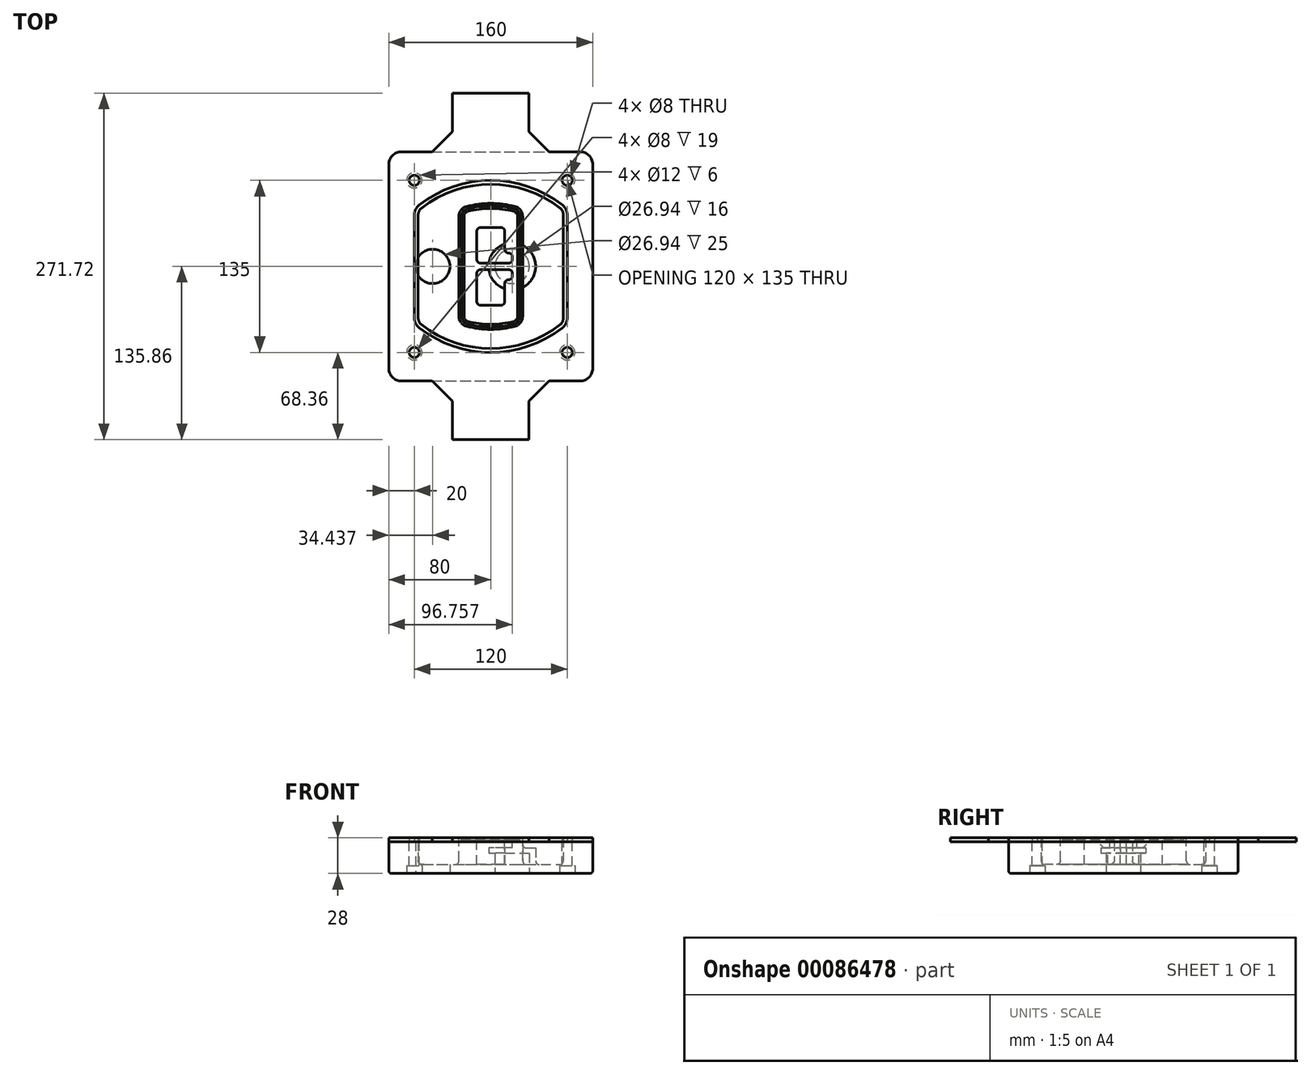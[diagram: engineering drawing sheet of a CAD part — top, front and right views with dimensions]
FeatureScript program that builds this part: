
annotation { "Feature Type Name" : "Feature", "Feature Type Description" : "" }
export const myFeature = defineFeature(function(context is Context, id is Id, definition is map)
    precondition{}
    {
        {
            var Q0;
            Q0=qCreatedBy(makeId("Top.planeOp"),FACE);
            var sketch = newSketch(context, id + "F0", { "sketchPlane" : qUnion([Q0])});
            skPoint(sketch, "E0.rect.middle", {"position": v(0, 0) * mm});
            skLineSegment(sketch, "E1.bottom", {"start": v(-70, -90) * mm, "end": v(70, -90) * mm});
            skLineSegment(sketch, "E1.top", {"start": v(-70, 90) * mm, "end": v(70, 90) * mm});
            skLineSegment(sketch, "E1.left", {"start": v(-80, -80) * mm, "end": v(-80, 80) * mm});
            skLineSegment(sketch, "E1.right", {"start": v(80, -80) * mm, "end": v(80, 80) * mm});
            skLineSegment(sketch, "E2", {"start": v(-80, 90) * mm, "end": v(80, -90) * mm, "construction": true});
            skLineSegment(sketch, "E3", {"start": v(80, 90) * mm, "end": v(-80, -90) * mm, "construction": true});
            skCircle(sketch, "E4", {"center": v(-60, 67.5) * mm, "radius": 4 * mm});
            skCircle(sketch, "E5", {"center": v(60, 67.5) * mm, "radius": 4 * mm});
            skCircle(sketch, "E6", {"center": v(60, -67.5) * mm, "radius": 4 * mm});
            skCircle(sketch, "E7", {"center": v(-60, -67.5) * mm, "radius": 4 * mm});
            skLineSegment(sketch, "E8", {"start": v(-60, 67.5) * mm, "end": v(60, 67.5) * mm, "construction": true});
            skLineSegment(sketch, "E9", {"start": v(60, 67.5) * mm, "end": v(60, -67.5) * mm, "construction": true});
            skLineSegment(sketch, "E10", {"start": v(60, -67.5) * mm, "end": v(-60, -67.5) * mm, "construction": true});
            skLineSegment(sketch, "E11", {"start": v(-60, -67.5) * mm, "end": v(-60, 67.5) * mm, "construction": true});
            skLineSegment(sketch, "E12", {"start": v(-60, 40.3) * mm, "end": v(-60, -40.3) * mm});
            skLineSegment(sketch, "E13", {"start": v(60, 40.3) * mm, "end": v(60, -40.3) * mm});
            skArc(sketch, "E14", {"start": v(56.15, 48.18) * mm, "mid": v(0, 67.5) * mm, "end": v(-56.15, 48.18) * mm});
            skArc(sketch, "E15", {"start": v(-56.15, -48.18) * mm, "mid": v(0, -67.5) * mm, "end": v(56.15, -48.18) * mm});
            skLineSegment(sketch, "E16", {"start": v(-60, 0) * mm, "end": v(60, 0) * mm, "construction": true});
            skPoint(sketch, "E17.visualSharp", {"position": v(-60, -45) * mm});
            skArc(sketch, "E17.filletArc", {"start": v(-60, -40.3) * mm, "mid": v(-58.99, -44.68) * mm, "end": v(-56.15, -48.18) * mm});
            skPoint(sketch, "E18.visualSharp", {"position": v(-60, 45) * mm});
            skArc(sketch, "E18.filletArc", {"start": v(-56.15, 48.18) * mm, "mid": v(-58.99, 44.68) * mm, "end": v(-60, 40.3) * mm});
            skPoint(sketch, "E19.visualSharp", {"position": v(60, 45) * mm});
            skArc(sketch, "E19.filletArc", {"start": v(60, 40.3) * mm, "mid": v(58.99, 44.68) * mm, "end": v(56.15, 48.18) * mm});
            skPoint(sketch, "E20.visualSharp", {"position": v(60, -45) * mm});
            skArc(sketch, "E20.filletArc", {"start": v(56.15, -48.18) * mm, "mid": v(58.99, -44.68) * mm, "end": v(60, -40.3) * mm});
            skPoint(sketch, "E21.visualSharp", {"position": v(-80, 90) * mm});
            skArc(sketch, "E21.filletArc", {"start": v(-70, 90) * mm, "mid": v(-77.07, 87.07) * mm, "end": v(-80, 80) * mm});
            skPoint(sketch, "E22.visualSharp", {"position": v(80, 90) * mm});
            skArc(sketch, "E22.filletArc", {"start": v(80, 80) * mm, "mid": v(77.07, 87.07) * mm, "end": v(70, 90) * mm});
            skPoint(sketch, "E23.visualSharp", {"position": v(80, -90) * mm});
            skArc(sketch, "E23.filletArc", {"start": v(70, -90) * mm, "mid": v(77.07, -87.07) * mm, "end": v(80, -80) * mm});
            skPoint(sketch, "E24.visualSharp", {"position": v(-80, -90) * mm});
            skArc(sketch, "E24.filletArc", {"start": v(-80, -80) * mm, "mid": v(-77.07, -87.07) * mm, "end": v(-70, -90) * mm});
            skArc(sketch, "E25.0", {"start": v(57, 40.3) * mm, "mid": v(56.3, 43.36) * mm, "end": v(54.3, 45.81) * mm});
            skLineSegment(sketch, "E25.1", {"start": v(57, 40.3) * mm, "end": v(57, -40.3) * mm});
            skArc(sketch, "E25.2", {"start": v(54.3, -45.81) * mm, "mid": v(56.3, -43.36) * mm, "end": v(57, -40.3) * mm});
            skArc(sketch, "E25.3", {"start": v(-54.3, -45.81) * mm, "mid": v(0, -64.5) * mm, "end": v(54.3, -45.81) * mm});
            skArc(sketch, "E25.4", {"start": v(-57, -40.3) * mm, "mid": v(-56.3, -43.36) * mm, "end": v(-54.3, -45.81) * mm});
            skArc(sketch, "E25.5", {"start": v(54.3, 45.81) * mm, "mid": v(0, 64.5) * mm, "end": v(-54.3, 45.81) * mm});
            skLineSegment(sketch, "E25.6", {"start": v(-57, 40.3) * mm, "end": v(-57, -40.3) * mm});
            skArc(sketch, "E25.7", {"start": v(-54.3, 45.81) * mm, "mid": v(-56.3, 43.36) * mm, "end": v(-57, 40.3) * mm});
            skArc(sketch, "E26.0", {"start": v(-58.62, 51.33) * mm, "mid": v(-62.58, 46.43) * mm, "end": v(-64, 40.3) * mm});
            skArc(sketch, "E26.1", {"start": v(58.62, 51.33) * mm, "mid": v(0, 71.5) * mm, "end": v(-58.62, 51.33) * mm});
            skArc(sketch, "E26.2", {"start": v(64, 40.3) * mm, "mid": v(62.58, 46.43) * mm, "end": v(58.62, 51.33) * mm});
            skLineSegment(sketch, "E26.3", {"start": v(64, 40.3) * mm, "end": v(64, -40.3) * mm});
            skArc(sketch, "E26.4", {"start": v(58.62, -51.33) * mm, "mid": v(62.58, -46.43) * mm, "end": v(64, -40.3) * mm});
            skLineSegment(sketch, "E26.5", {"start": v(-64, 40.3) * mm, "end": v(-64, -40.3) * mm});
            skArc(sketch, "E26.6", {"start": v(-58.62, -51.33) * mm, "mid": v(0, -71.5) * mm, "end": v(58.62, -51.33) * mm});
            skArc(sketch, "E26.7", {"start": v(-64, -40.3) * mm, "mid": v(-62.58, -46.43) * mm, "end": v(-58.62, -51.33) * mm});
            skSolve(sketch);
        }
        {
            var Q0;
            Q0=makeQuery(id+"F0.imprint","IMPRINT",FACE,{"disambiguationData":[TD([[makeQuery(id+"F0.imprint","IMPRINT",EDGE,{"derivedFrom":sQuery(id+"F0.wireOp",EDGE,"E1.bottom")}),1.0]])]});
            var Q1;
            Q1=makeQuery(id+"F0.imprint","IMPRINT",FACE,{"disambiguationData":[TD([[makeQuery(id+"F0.imprint","IMPRINT",EDGE,{"derivedFrom":sQuery(id+"F0.wireOp",EDGE,"E12")}),1.0]])]});
            var Q2;
            Q2=makeQuery(id+"F0.imprint","IMPRINT",FACE,{"disambiguationData":[TD([[makeQuery(id+"F0.imprint","IMPRINT",EDGE,{"derivedFrom":sQuery(id+"F0.wireOp",EDGE,"E25.0")}),1.0]])]});
            var Q3;
            Q3=makeQuery(id+"F0.imprint","IMPRINT",FACE,{"disambiguationData":[TD([[makeQuery(id+"F0.imprint","IMPRINT",EDGE,{"derivedFrom":sQuery(id+"F0.wireOp",EDGE,"E12")}),-1.0]])]});
            extrude(context, id + "F1", {"entities" : qUnion([Q0, Q1, Q2, Q3]), "oppositeDirection" : true, "depth" : 25 * mm});
        }
        {
            var Q0;
            Q0=makeQuery(id+"F0.imprint","IMPRINT",FACE,{"disambiguationData":[TD([[makeQuery(id+"F0.imprint","IMPRINT",EDGE,{"derivedFrom":sQuery(id+"F0.wireOp",EDGE,"E12")}),1.0]])]});
            extrude(context, id + "F2", {"entities" : qUnion([Q0]), "operationType" : NewBodyOperationType.ADD, "depth" : 3 * mm});
        }
        {
            var Q0;
            Q0=makeQuery(id+"F0.imprint","IMPRINT",FACE,{"disambiguationData":[TD([[makeQuery(id+"F0.imprint","IMPRINT",EDGE,{"derivedFrom":sQuery(id+"F0.wireOp",EDGE,"E25.0")}),1.0]])]});
            extrude(context, id + "F3", {"entities" : qUnion([Q0]), "operationType" : NewBodyOperationType.REMOVE, "oppositeDirection" : true, "depth" : 18 * mm});
        }
        {
            var Q0;
            Q0=makeQuery(id+"F2.opExtrude","CAP_FACE",FACE,{"disambiguationData":[OSD([sQuery(id+"F0.wireOp",EDGE,"E12"),sQuery(id+"F0.wireOp",EDGE,"E13"),sQuery(id+"F0.wireOp",EDGE,"E14"),sQuery(id+"F0.wireOp",EDGE,"E15"),sQuery(id+"F0.wireOp",EDGE,"E17.filletArc"),sQuery(id+"F0.wireOp",EDGE,"E18.filletArc"),sQuery(id+"F0.wireOp",EDGE,"E19.filletArc"),sQuery(id+"F0.wireOp",EDGE,"E20.filletArc"),sQuery(id+"F0.wireOp",EDGE,"E25.0"),sQuery(id+"F0.wireOp",EDGE,"E25.1"),sQuery(id+"F0.wireOp",EDGE,"E25.2"),sQuery(id+"F0.wireOp",EDGE,"E25.3"),sQuery(id+"F0.wireOp",EDGE,"E25.4"),sQuery(id+"F0.wireOp",EDGE,"E25.5"),sQuery(id+"F0.wireOp",EDGE,"E25.6"),sQuery(id+"F0.wireOp",EDGE,"E25.7")])],"isStart":false});
            var sketch = newSketch(context, id + "F4", { "sketchPlane" : qUnion([Q0])});
            skArc(sketch, "E27.0", {"start": v(-19.08, -46.97) * mm, "mid": v(0, -49.5) * mm, "end": v(19.08, -46.97) * mm});
            skArc(sketch, "E28.0", {"start": v(19.08, 46.97) * mm, "mid": v(0, 49.5) * mm, "end": v(-19.08, 46.97) * mm});
            skLineSegment(sketch, "E29", {"start": v(-25, 39.25) * mm, "end": v(-25, -39.25) * mm});
            skLineSegment(sketch, "E30", {"start": v(25, 39.25) * mm, "end": v(25, -39.25) * mm});
            skLineSegment(sketch, "E31", {"start": v(-25, 45.1) * mm, "end": v(25, 45.1) * mm, "construction": true});
            skLineSegment(sketch, "E32", {"start": v(-25, -45.1) * mm, "end": v(25, -45.1) * mm, "construction": true});
            skPoint(sketch, "E33.visualSharp", {"position": v(-25, 45.1) * mm});
            skArc(sketch, "E33.filletArc", {"start": v(-19.08, 46.97) * mm, "mid": v(-23.35, 44.11) * mm, "end": v(-25, 39.25) * mm});
            skPoint(sketch, "E34.visualSharp", {"position": v(25, 45.1) * mm});
            skArc(sketch, "E34.filletArc", {"start": v(25, 39.25) * mm, "mid": v(23.35, 44.11) * mm, "end": v(19.08, 46.97) * mm});
            skPoint(sketch, "E35.visualSharp", {"position": v(25, -45.1) * mm});
            skArc(sketch, "E35.filletArc", {"start": v(19.08, -46.97) * mm, "mid": v(23.35, -44.11) * mm, "end": v(25, -39.25) * mm});
            skPoint(sketch, "E36.visualSharp", {"position": v(-25, -45.1) * mm});
            skArc(sketch, "E36.filletArc", {"start": v(-25, -39.25) * mm, "mid": v(-23.35, -44.11) * mm, "end": v(-19.08, -46.97) * mm});
            skArc(sketch, "E37.0", {"start": v(54.3, 45.81) * mm, "mid": v(0, 64.5) * mm, "end": v(-54.3, 45.81) * mm});
            skArc(sketch, "E37.1", {"start": v(-54.3, 45.81) * mm, "mid": v(-56.3, 43.36) * mm, "end": v(-57, 40.3) * mm});
            skLineSegment(sketch, "E37.2", {"start": v(-57, 40.3) * mm, "end": v(-57, -40.3) * mm});
            skArc(sketch, "E37.3", {"start": v(-57, -40.3) * mm, "mid": v(-56.3, -43.36) * mm, "end": v(-54.3, -45.81) * mm});
            skArc(sketch, "E37.4", {"start": v(-54.3, -45.81) * mm, "mid": v(0, -64.5) * mm, "end": v(54.3, -45.81) * mm});
            skArc(sketch, "E37.5", {"start": v(54.3, -45.81) * mm, "mid": v(56.3, -43.36) * mm, "end": v(57, -40.3) * mm});
            skLineSegment(sketch, "E37.6", {"start": v(57, 40.3) * mm, "end": v(57, -40.3) * mm});
            skArc(sketch, "E37.7", {"start": v(57, 40.3) * mm, "mid": v(56.3, 43.36) * mm, "end": v(54.3, 45.81) * mm});
            skLineSegment(sketch, "E38.0", {"start": v(23, 39.25) * mm, "end": v(23, -39.25) * mm});
            skArc(sketch, "E38.1", {"start": v(18.56, -45.04) * mm, "mid": v(21.76, -42.9) * mm, "end": v(23, -39.25) * mm});
            skArc(sketch, "E38.2", {"start": v(-18.56, -45.04) * mm, "mid": v(0, -47.5) * mm, "end": v(18.56, -45.04) * mm});
            skArc(sketch, "E38.3", {"start": v(-23, -39.25) * mm, "mid": v(-21.76, -42.9) * mm, "end": v(-18.56, -45.04) * mm});
            skLineSegment(sketch, "E38.4", {"start": v(-23, 39.25) * mm, "end": v(-23, -39.25) * mm});
            skArc(sketch, "E38.5", {"start": v(23, 39.25) * mm, "mid": v(21.76, 42.9) * mm, "end": v(18.56, 45.04) * mm});
            skArc(sketch, "E38.6", {"start": v(-18.56, 45.04) * mm, "mid": v(-21.76, 42.9) * mm, "end": v(-23, 39.25) * mm});
            skArc(sketch, "E38.7", {"start": v(18.56, 45.04) * mm, "mid": v(0, 47.5) * mm, "end": v(-18.56, 45.04) * mm});
            skArc(sketch, "E39.0", {"start": v(21, 39.25) * mm, "mid": v(20.18, 41.68) * mm, "end": v(18.04, 43.1) * mm});
            skLineSegment(sketch, "E39.1", {"start": v(21, 39.25) * mm, "end": v(21, -39.25) * mm});
            skArc(sketch, "E39.2", {"start": v(18.04, -43.1) * mm, "mid": v(20.18, -41.68) * mm, "end": v(21, -39.25) * mm});
            skArc(sketch, "E39.3", {"start": v(-18.04, -43.1) * mm, "mid": v(0, -45.5) * mm, "end": v(18.04, -43.1) * mm});
            skArc(sketch, "E39.4", {"start": v(-21, -39.25) * mm, "mid": v(-20.18, -41.68) * mm, "end": v(-18.04, -43.1) * mm});
            skArc(sketch, "E39.5", {"start": v(18.04, 43.1) * mm, "mid": v(0, 45.5) * mm, "end": v(-18.04, 43.1) * mm});
            skLineSegment(sketch, "E39.6", {"start": v(-21, 39.25) * mm, "end": v(-21, -39.25) * mm});
            skArc(sketch, "E39.7", {"start": v(-18.04, 43.1) * mm, "mid": v(-20.18, 41.68) * mm, "end": v(-21, 39.25) * mm});
            skLineSegment(sketch, "E40", {"start": v(-25, 0) * mm, "end": v(25, 0) * mm, "construction": true});
            skLineSegment(sketch, "E41", {"start": v(-11, 5.5) * mm, "end": v(-11, 27.5) * mm});
            skLineSegment(sketch, "E42", {"start": v(-8, 30.5) * mm, "end": v(8, 30.5) * mm});
            skLineSegment(sketch, "E43", {"start": v(11, 27.5) * mm, "end": v(11, 13.5) * mm});
            skLineSegment(sketch, "E44", {"start": v(14, 10.5) * mm, "end": v(14, 10.5) * mm});
            skLineSegment(sketch, "E45", {"start": v(17, 7.5) * mm, "end": v(17, 5.5) * mm});
            skLineSegment(sketch, "E46", {"start": v(14, 2.5) * mm, "end": v(-8, 2.5) * mm});
            skPoint(sketch, "E47.visualSharp", {"position": v(-11, 30.5) * mm});
            skArc(sketch, "E47.filletArc", {"start": v(-8, 30.5) * mm, "mid": v(-10.12, 29.62) * mm, "end": v(-11, 27.5) * mm});
            skPoint(sketch, "E48.visualSharp", {"position": v(11, 30.5) * mm});
            skArc(sketch, "E48.filletArc", {"start": v(11, 27.5) * mm, "mid": v(10.12, 29.62) * mm, "end": v(8, 30.5) * mm});
            skPoint(sketch, "E49.visualSharp", {"position": v(11, 10.5) * mm});
            skArc(sketch, "E49.filletArc", {"start": v(11, 13.5) * mm, "mid": v(11.88, 11.38) * mm, "end": v(14, 10.5) * mm});
            skPoint(sketch, "E50.visualSharp", {"position": v(17, 10.5) * mm});
            skArc(sketch, "E50.filletArc", {"start": v(17, 7.5) * mm, "mid": v(16.12, 9.62) * mm, "end": v(14, 10.5) * mm});
            skPoint(sketch, "E51.visualSharp", {"position": v(17, 2.5) * mm});
            skArc(sketch, "E51.filletArc", {"start": v(14, 2.5) * mm, "mid": v(16.12, 3.38) * mm, "end": v(17, 5.5) * mm});
            skPoint(sketch, "E52.visualSharp", {"position": v(-11, 2.5) * mm});
            skArc(sketch, "E52.filletArc", {"start": v(-11, 5.5) * mm, "mid": v(-10.12, 3.38) * mm, "end": v(-8, 2.5) * mm});
            skLineSegment(sketch, "E53.0.MirrorCS", {"start": v(14, -2.5) * mm, "end": v(-8, -2.5) * mm});
            skArc(sketch, "E54.0.MirrorCS", {"start": v(-11, -5.5) * mm, "mid": v(-10.12, -3.38) * mm, "end": v(-8, -2.5) * mm});
            skLineSegment(sketch, "E55.0.MirrorCS", {"start": v(-11, -5.5) * mm, "end": v(-11, -27.5) * mm});
            skArc(sketch, "E56.0.MirrorCS", {"start": v(-8, -30.5) * mm, "mid": v(-10.12, -29.62) * mm, "end": v(-11, -27.5) * mm});
            skLineSegment(sketch, "E57.0.MirrorCS", {"start": v(-8, -30.5) * mm, "end": v(8, -30.5) * mm});
            skArc(sketch, "E58.0.MirrorCS", {"start": v(11, -27.5) * mm, "mid": v(10.12, -29.62) * mm, "end": v(8, -30.5) * mm});
            skLineSegment(sketch, "E59.0.MirrorCS", {"start": v(11, -27.5) * mm, "end": v(11, -13.5) * mm});
            skArc(sketch, "E60.0.MirrorCS", {"start": v(11, -13.5) * mm, "mid": v(11.88, -11.38) * mm, "end": v(14, -10.5) * mm});
            skArc(sketch, "E61.0.MirrorCS", {"start": v(17, -7.5) * mm, "mid": v(16.12, -9.62) * mm, "end": v(14, -10.5) * mm});
            skLineSegment(sketch, "E62.0.MirrorCS", {"start": v(17, -7.5) * mm, "end": v(17, -5.5) * mm});
            skArc(sketch, "E63.0.MirrorCS", {"start": v(14, -2.5) * mm, "mid": v(16.12, -3.38) * mm, "end": v(17, -5.5) * mm});
            skSolve(sketch);
        }
        {
            var Q0;
            Q0=makeQuery(id+"F4.imprint","IMPRINT",FACE,{"disambiguationData":[TD([[makeQuery(id+"F4.imprint","IMPRINT",EDGE,{"derivedFrom":sQuery(id+"F4.wireOp",EDGE,"E27.0")}),1.0]])]});
            var Q1;
            Q1=makeQuery(id+"F4.imprint","IMPRINT",FACE,{"disambiguationData":[TD([[makeQuery(id+"F4.imprint","IMPRINT",EDGE,{"derivedFrom":sQuery(id+"F4.wireOp",EDGE,"E38.0")}),-1.0]])]});
            var Q2;
            Q2=makeQuery(id+"F4.imprint","IMPRINT",FACE,{"disambiguationData":[TD([[makeQuery(id+"F4.imprint","IMPRINT",EDGE,{"derivedFrom":sQuery(id+"F4.wireOp",EDGE,"E39.0")}),1.0]])]});
            extrude(context, id + "F5", {"entities" : qUnion([Q0, Q1, Q2]), "operationType" : NewBodyOperationType.ADD, "endBound" : BoundingType.UP_TO_NEXT, "oppositeDirection" : true, "depth" : 25 * mm});
        }
        {
            var Q0;
            Q0=makeQuery(id+"F4.imprint","IMPRINT",FACE,{"disambiguationData":[TD([[makeQuery(id+"F4.imprint","IMPRINT",EDGE,{"derivedFrom":sQuery(id+"F4.wireOp",EDGE,"E38.0")}),-1.0]])]});
            extrude(context, id + "F6", {"entities" : qUnion([Q0]), "operationType" : NewBodyOperationType.REMOVE, "oppositeDirection" : true, "depth" : 2 * mm});
        }
        {
            var Q0;
            Q0=makeQuery(id+"F1.opExtrude","CAP_FACE",FACE,{"disambiguationData":[OSD([sQuery(id+"F0.wireOp",EDGE,"E1.bottom"),sQuery(id+"F0.wireOp",EDGE,"E1.top"),sQuery(id+"F0.wireOp",EDGE,"E1.left"),sQuery(id+"F0.wireOp",EDGE,"E1.right"),sQuery(id+"F0.wireOp",EDGE,"E4"),sQuery(id+"F0.wireOp",EDGE,"E5"),sQuery(id+"F0.wireOp",EDGE,"E6"),sQuery(id+"F0.wireOp",EDGE,"E7"),sQuery(id+"F0.wireOp",EDGE,"E21.filletArc"),sQuery(id+"F0.wireOp",EDGE,"E22.filletArc"),sQuery(id+"F0.wireOp",EDGE,"E23.filletArc"),sQuery(id+"F0.wireOp",EDGE,"E24.filletArc")])],"isStart":false});
            var sketch = newSketch(context, id + "F7", { "sketchPlane" : qUnion([Q0])});
            skCircle(sketch, "E64", {"center": v(16.76, 0) * mm, "radius": 13.47 * mm});
            skCircle(sketch, "E65", {"center": v(-45.56, 0) * mm, "radius": 13.47 * mm});
            skLineSegment(sketch, "E66", {"start": v(80, 0) * mm, "end": v(-80, 0) * mm});
            skCircle(sketch, "E67", {"center": v(16.76, 0) * mm, "radius": 18.47 * mm});
            skCircle(sketch, "E68", {"center": v(60, -67.5) * mm, "radius": 6 * mm});
            skCircle(sketch, "E69", {"center": v(-60, -67.5) * mm, "radius": 6 * mm});
            skCircle(sketch, "E70", {"center": v(-60, 67.5) * mm, "radius": 6 * mm});
            skCircle(sketch, "E71", {"center": v(60, 67.5) * mm, "radius": 6 * mm});
            skSolve(sketch);
        }
        {
            var Q0;
            {var subQ1=sQuery(id+"F7.wireOp",EDGE,"E66");var subQ4=sQuery(id+"F7.wireOp",EDGE,"E64");var subQ6=makeQuery(id+"F7.imprint","INTERSECT",VERTEX,{"disambiguationData":[OD(0.0)],"derivedFrom":[subQ4,subQ1]});Q0=makeQuery(id+"F7.imprint","IMPRINT",FACE,{"disambiguationData":[TD([[makeQuery(id+"F7.imprint","IMPRINT",EDGE,{"disambiguationData":[TD([[subQ6,-1.0]])],"derivedFrom":subQ4}),-1.0]])]});}
            var Q1;
            {var subQ0=sQuery(id+"F7.wireOp",EDGE,"E66");var subQ1=sQuery(id+"F7.wireOp",EDGE,"E64");var subQ3=makeQuery(id+"F7.imprint","INTERSECT",VERTEX,{"disambiguationData":[OD(0.0)],"derivedFrom":[subQ1,subQ0]});Q1=makeQuery(id+"F7.imprint","IMPRINT",FACE,{"disambiguationData":[TD([[makeQuery(id+"F7.imprint","IMPRINT",EDGE,{"disambiguationData":[TD([[subQ3,-1.0]])],"derivedFrom":subQ1}),1.0]])]});}
            var Q2;
            {var subQ0=sQuery(id+"F7.wireOp",EDGE,"E66");var subQ1=sQuery(id+"F7.wireOp",EDGE,"E64");var subQ3=makeQuery(id+"F7.imprint","INTERSECT",VERTEX,{"disambiguationData":[OD(0.0)],"derivedFrom":[subQ1,subQ0]});Q2=makeQuery(id+"F7.imprint","IMPRINT",FACE,{"disambiguationData":[TD([[makeQuery(id+"F7.imprint","IMPRINT",EDGE,{"disambiguationData":[TD([[subQ3,1.0]])],"derivedFrom":subQ1}),1.0]])]});}
            var Q3;
            {var subQ1=sQuery(id+"F7.wireOp",EDGE,"E66");var subQ4=sQuery(id+"F7.wireOp",EDGE,"E64");var subQ6=makeQuery(id+"F7.imprint","INTERSECT",VERTEX,{"disambiguationData":[OD(0.0)],"derivedFrom":[subQ4,subQ1]});Q3=makeQuery(id+"F7.imprint","IMPRINT",FACE,{"disambiguationData":[TD([[makeQuery(id+"F7.imprint","IMPRINT",EDGE,{"disambiguationData":[TD([[subQ6,1.0]])],"derivedFrom":subQ4}),-1.0]])]});}
            extrude(context, id + "F8", {"entities" : qUnion([Q0, Q1, Q2, Q3]), "operationType" : NewBodyOperationType.ADD, "oppositeDirection" : true, "depth" : 20 * mm});
        }
        {
            var Q0;
            {var subQ0=sQuery(id+"F7.wireOp",EDGE,"E66");var subQ1=sQuery(id+"F7.wireOp",EDGE,"E64");var subQ3=makeQuery(id+"F7.imprint","INTERSECT",VERTEX,{"disambiguationData":[OD(0.0)],"derivedFrom":[subQ1,subQ0]});Q0=makeQuery(id+"F7.imprint","IMPRINT",FACE,{"disambiguationData":[TD([[makeQuery(id+"F7.imprint","IMPRINT",EDGE,{"disambiguationData":[TD([[subQ3,-1.0]])],"derivedFrom":subQ1}),1.0]])]});}
            var Q1;
            {var subQ0=sQuery(id+"F7.wireOp",EDGE,"E66");var subQ1=sQuery(id+"F7.wireOp",EDGE,"E64");var subQ3=makeQuery(id+"F7.imprint","INTERSECT",VERTEX,{"disambiguationData":[OD(0.0)],"derivedFrom":[subQ1,subQ0]});Q1=makeQuery(id+"F7.imprint","IMPRINT",FACE,{"disambiguationData":[TD([[makeQuery(id+"F7.imprint","IMPRINT",EDGE,{"disambiguationData":[TD([[subQ3,1.0]])],"derivedFrom":subQ1}),1.0]])]});}
            extrude(context, id + "F9", {"entities" : qUnion([Q0, Q1]), "operationType" : NewBodyOperationType.REMOVE, "oppositeDirection" : true, "depth" : 16 * mm});
        }
        {
            var Q0;
            {var subQ0=sQuery(id+"F7.wireOp",EDGE,"E66");var subQ1=sQuery(id+"F7.wireOp",EDGE,"E65");var subQ3=makeQuery(id+"F7.imprint","INTERSECT",VERTEX,{"disambiguationData":[OD(0.0)],"derivedFrom":[subQ1,subQ0]});Q0=makeQuery(id+"F7.imprint","IMPRINT",FACE,{"disambiguationData":[TD([[makeQuery(id+"F7.imprint","IMPRINT",EDGE,{"disambiguationData":[TD([[subQ3,-1.0]])],"derivedFrom":subQ1}),1.0]])]});}
            var Q1;
            {var subQ0=sQuery(id+"F7.wireOp",EDGE,"E66");var subQ1=sQuery(id+"F7.wireOp",EDGE,"E65");var subQ3=makeQuery(id+"F7.imprint","INTERSECT",VERTEX,{"disambiguationData":[OD(0.0)],"derivedFrom":[subQ1,subQ0]});Q1=makeQuery(id+"F7.imprint","IMPRINT",FACE,{"disambiguationData":[TD([[makeQuery(id+"F7.imprint","IMPRINT",EDGE,{"disambiguationData":[TD([[subQ3,1.0]])],"derivedFrom":subQ1}),1.0]])]});}
            extrude(context, id + "F10", {"entities" : qUnion([Q0, Q1]), "operationType" : NewBodyOperationType.REMOVE, "oppositeDirection" : true, "depth" : 25 * mm});
        }
        {
            var Q0;
            Q0=makeQuery(id+"F7.imprint","IMPRINT",FACE,{"disambiguationData":[TD([[makeQuery(id+"F7.imprint","IMPRINT",EDGE,{"derivedFrom":sQuery(id+"F7.wireOp",EDGE,"E68")}),1.0]])]});
            var Q1;
            Q1=makeQuery(id+"F7.imprint","IMPRINT",FACE,{"disambiguationData":[TD([[makeQuery(id+"F7.imprint","IMPRINT",EDGE,{"derivedFrom":makeQuery(id+"F1.opExtrude","CAP_EDGE",EDGE,{"disambiguationData":[OSD([sQuery(id+"F0.wireOp",EDGE,"E5")])],"isStart":false})}),-1.0]])]});
            var Q2;
            Q2=makeQuery(id+"F7.imprint","IMPRINT",FACE,{"disambiguationData":[TD([[makeQuery(id+"F7.imprint","IMPRINT",EDGE,{"derivedFrom":sQuery(id+"F7.wireOp",EDGE,"E69")}),1.0]])]});
            var Q3;
            Q3=makeQuery(id+"F7.imprint","IMPRINT",FACE,{"disambiguationData":[TD([[makeQuery(id+"F7.imprint","IMPRINT",EDGE,{"derivedFrom":makeQuery(id+"F1.opExtrude","CAP_EDGE",EDGE,{"disambiguationData":[OSD([sQuery(id+"F0.wireOp",EDGE,"E4")])],"isStart":false})}),-1.0]])]});
            var Q4;
            Q4=makeQuery(id+"F7.imprint","IMPRINT",FACE,{"disambiguationData":[TD([[makeQuery(id+"F7.imprint","IMPRINT",EDGE,{"derivedFrom":sQuery(id+"F7.wireOp",EDGE,"E70")}),1.0]])]});
            var Q5;
            Q5=makeQuery(id+"F7.imprint","IMPRINT",FACE,{"disambiguationData":[TD([[makeQuery(id+"F7.imprint","IMPRINT",EDGE,{"derivedFrom":makeQuery(id+"F1.opExtrude","CAP_EDGE",EDGE,{"disambiguationData":[OSD([sQuery(id+"F0.wireOp",EDGE,"E7")])],"isStart":false})}),-1.0]])]});
            var Q6;
            Q6=makeQuery(id+"F7.imprint","IMPRINT",FACE,{"disambiguationData":[TD([[makeQuery(id+"F7.imprint","IMPRINT",EDGE,{"derivedFrom":sQuery(id+"F7.wireOp",EDGE,"E71")}),1.0]])]});
            var Q7;
            Q7=makeQuery(id+"F7.imprint","IMPRINT",FACE,{"disambiguationData":[TD([[makeQuery(id+"F7.imprint","IMPRINT",EDGE,{"derivedFrom":makeQuery(id+"F1.opExtrude","CAP_EDGE",EDGE,{"disambiguationData":[OSD([sQuery(id+"F0.wireOp",EDGE,"E6")])],"isStart":false})}),-1.0]])]});
            extrude(context, id + "F11", {"entities" : qUnion([Q0, Q1, Q2, Q3, Q4, Q5, Q6, Q7]), "operationType" : NewBodyOperationType.REMOVE, "oppositeDirection" : true, "depth" : 6 * mm});
        }
        {
            var Q0;
            Q0=makeQuery(id+"F9.boolean.opBoolean","COPY",FACE,{"derivedFrom":makeQuery(id+"F9.opExtrude","CAP_FACE",FACE,{"disambiguationData":[OSD([sQuery(id+"F7.wireOp",EDGE,"E64")])],"isStart":false})});
            var sketch = newSketch(context, id + "F12", { "sketchPlane" : qUnion([Q0])});
            skArc(sketch, "E72.0", {"start": v(11, 17.55) * mm, "mid": v(2.57, 11.82) * mm, "end": v(-1.54, 2.5) * mm});
            skArc(sketch, "E72.1", {"start": v(-1.54, -2.5) * mm, "mid": v(2.57, -11.82) * mm, "end": v(11, -17.55) * mm});
            skLineSegment(sketch, "E73", {"start": v(-1.54, -2.5) * mm, "end": v(14, -2.5) * mm});
            skLineSegment(sketch, "E74.0", {"start": v(14, 2.5) * mm, "end": v(-1.54, 2.5) * mm});
            skArc(sketch, "E74.1", {"start": v(14, 2.5) * mm, "mid": v(16.12, 3.38) * mm, "end": v(17, 5.5) * mm});
            skLineSegment(sketch, "E74.2", {"start": v(17, 7.5) * mm, "end": v(17, 5.5) * mm});
            skArc(sketch, "E74.3", {"start": v(17, 7.5) * mm, "mid": v(16.12, 9.62) * mm, "end": v(14, 10.5) * mm});
            skArc(sketch, "E74.4", {"start": v(11, 13.5) * mm, "mid": v(11.88, 11.38) * mm, "end": v(14, 10.5) * mm});
            skLineSegment(sketch, "E74.5", {"start": v(11, 17.55) * mm, "end": v(11, 13.5) * mm});
            skLineSegment(sketch, "E74.7", {"start": v(14, -2.5) * mm, "end": v(-1.54, -2.5) * mm});
            skArc(sketch, "E74.8", {"start": v(14, -2.5) * mm, "mid": v(16.12, -3.38) * mm, "end": v(17, -5.5) * mm});
            skLineSegment(sketch, "E74.9", {"start": v(17, -7.5) * mm, "end": v(17, -5.5) * mm});
            skArc(sketch, "E74.10", {"start": v(17, -7.5) * mm, "mid": v(16.12, -9.62) * mm, "end": v(14, -10.5) * mm});
            skArc(sketch, "E74.11", {"start": v(11, -13.5) * mm, "mid": v(11.88, -11.38) * mm, "end": v(14, -10.5) * mm});
            skLineSegment(sketch, "E74.12", {"start": v(11, -17.55) * mm, "end": v(11, -13.5) * mm});
            skPoint(sketch, "E75.orphan", {"position": v(11, -27.5) * mm});
            skPoint(sketch, "E76.orphan", {"position": v(-8, -2.5) * mm});
            skPoint(sketch, "E77.orphan", {"position": v(-8, 2.5) * mm});
            skPoint(sketch, "E78.orphan", {"position": v(11, 27.5) * mm});
            skSolve(sketch);
        }
        {
            var Q0;
            {var subQ7=sQuery(id+"F12.wireOp",EDGE,"E72.0");var subQ14=sQuery(id+"F12.wireOp",EDGE,"E72.1");var subQ16=sQuery(id+"F12.wireOp",EDGE,"E74.1");var subQ18=sQuery(id+"F12.wireOp",EDGE,"E74.8");Q0=qUnion([makeQuery(id+"F12.imprint","IMPRINT",FACE,{"disambiguationData":[TD([[makeQuery(id+"F12.imprint","IMPRINT",EDGE,{"derivedFrom":subQ7}),1.0]])]}),makeQuery(id+"F12.imprint","IMPRINT",FACE,{"disambiguationData":[TD([[makeQuery(id+"F12.imprint","IMPRINT",EDGE,{"derivedFrom":subQ14}),1.0]])]}),makeQuery(id+"F12.imprint","IMPRINT",FACE,{"disambiguationData":[TD([[makeQuery(id+"F12.imprint","IMPRINT",EDGE,{"derivedFrom":subQ16}),1.0]])]}),makeQuery(id+"F12.imprint","IMPRINT",FACE,{"disambiguationData":[TD([[makeQuery(id+"F12.imprint","IMPRINT",EDGE,{"derivedFrom":subQ18}),-1.0]])]})]);}
            var Q1;
            Q1=makeQuery(id+"F5.boolean.opBoolean","SPLIT",FACE,{"disambiguationData":[TD([makeQuery(id+"F5.opExtrude","SWEPT_FACE",FACE,{"disambiguationData":[OSD([sQuery(id+"F4.wireOp",EDGE,"E41")])]})])],"derivedFrom":makeQuery(id+"F3.boolean.opBoolean","COPY",FACE,{"derivedFrom":makeQuery(id+"F3.opExtrude","CAP_FACE",FACE,{"disambiguationData":[OSD([sQuery(id+"F0.wireOp",EDGE,"E25.0"),sQuery(id+"F0.wireOp",EDGE,"E25.1"),sQuery(id+"F0.wireOp",EDGE,"E25.2"),sQuery(id+"F0.wireOp",EDGE,"E25.3"),sQuery(id+"F0.wireOp",EDGE,"E25.4"),sQuery(id+"F0.wireOp",EDGE,"E25.5"),sQuery(id+"F0.wireOp",EDGE,"E25.6"),sQuery(id+"F0.wireOp",EDGE,"E25.7")])],"isStart":false})})});
            extrude(context, id + "F13", {"entities" : qUnion([Q0]), "operationType" : NewBodyOperationType.REMOVE, "endBound" : BoundingType.UP_TO_SURFACE, "endBoundEntityFace" : qUnion([Q1]), "depth" : 25 * mm});
        }
        {
            var Q0;
            Q0=makeQuery(id+"F3.boolean.opBoolean","COPY",EDGE,{"derivedFrom":makeQuery(id+"F3.opExtrude","CAP_EDGE",EDGE,{"disambiguationData":[OSD([sQuery(id+"F0.wireOp",EDGE,"E25.6")])],"isStart":false})});
            var Q1;
            Q1=makeQuery(id+"F8.boolean.opBoolean","INTERSECT",EDGE,{"derivedFrom":[makeQuery(id+"F5.opExtrude","SWEPT_FACE",FACE,{"disambiguationData":[OSD([sQuery(id+"F4.wireOp",EDGE,"E30")])]}),makeQuery(id+"F8.opExtrude","CAP_FACE",FACE,{"disambiguationData":[OSD([sQuery(id+"F7.wireOp",EDGE,"E67")])],"isStart":false})]});
            var Q2;
            Q2=makeQuery(id+"F8.boolean.opBoolean","INTERSECT",EDGE,{"disambiguationData":[OD(1.0)],"derivedFrom":[makeQuery(id+"F5.opExtrude","SWEPT_FACE",FACE,{"disambiguationData":[OSD([sQuery(id+"F4.wireOp",EDGE,"E30")])]}),makeQuery(id+"F8.opExtrude","SWEPT_FACE",FACE,{"disambiguationData":[OSD([sQuery(id+"F7.wireOp",EDGE,"E67")])]})]});
            var Q3;
            {var subQ0=sQuery(id+"F4.wireOp",EDGE,"E30");Q3=makeQuery(id+"F8.boolean.opBoolean","SPLIT",EDGE,{"disambiguationData":[TD([makeQuery(id+"F5.opExtrude","SWEPT_FACE",FACE,{"disambiguationData":[OSD([sQuery(id+"F4.wireOp",EDGE,"E35.filletArc")])]})])],"derivedFrom":makeQuery(id+"F5.opExtrude","CAP_EDGE",EDGE,{"disambiguationData":[OSD([subQ0])],"isStart":false})});}
            var Q4;
            {var subQ0=sQuery(id+"F0.wireOp",EDGE,"E25.7");var subQ1=sQuery(id+"F0.wireOp",EDGE,"E25.1");var subQ2=sQuery(id+"F0.wireOp",EDGE,"E25.6");var subQ3=sQuery(id+"F0.wireOp",EDGE,"E25.5");var subQ4=sQuery(id+"F0.wireOp",EDGE,"E25.4");var subQ5=sQuery(id+"F0.wireOp",EDGE,"E25.0");var subQ6=sQuery(id+"F0.wireOp",EDGE,"E25.2");var subQ7=sQuery(id+"F0.wireOp",EDGE,"E25.3");Q4=makeQuery(id+"F8.boolean.opBoolean","INTERSECT",EDGE,{"derivedFrom":[makeQuery(id+"F5.boolean.opBoolean","SPLIT",FACE,{"disambiguationData":[TD([makeQuery(id+"F2.opExtrude","SWEPT_FACE",FACE,{"disambiguationData":[OSD([subQ5])]})])],"derivedFrom":makeQuery(id+"F3.boolean.opBoolean","COPY",FACE,{"derivedFrom":makeQuery(id+"F3.opExtrude","CAP_FACE",FACE,{"disambiguationData":[OSD([subQ5,subQ1,subQ6,subQ7,subQ4,subQ3,subQ2,subQ0])],"isStart":false})})}),makeQuery(id+"F8.opExtrude","SWEPT_FACE",FACE,{"disambiguationData":[OSD([sQuery(id+"F7.wireOp",EDGE,"E67")])]})]});}
            var Q5;
            Q5=makeQuery(id+"F8.boolean.opBoolean","INTERSECT",EDGE,{"disambiguationData":[OD(0.0)],"derivedFrom":[makeQuery(id+"F5.opExtrude","SWEPT_FACE",FACE,{"disambiguationData":[OSD([sQuery(id+"F4.wireOp",EDGE,"E30")])]}),makeQuery(id+"F8.opExtrude","SWEPT_FACE",FACE,{"disambiguationData":[OSD([sQuery(id+"F7.wireOp",EDGE,"E67")])]})]});
            fillet(context, id + "F14", {"entities" : qUnion([Q0, Q1, Q2, Q3, Q4, Q5]), "radius" : 3 * mm, "tangentPropagation" : true, "allowEdgeOverflow" : false});
        }
        {
            var Q0;
            Q0=makeQuery(id+"F1.opExtrude","CAP_EDGE",EDGE,{"disambiguationData":[OSD([sQuery(id+"F0.wireOp",EDGE,"E1.bottom")])],"isStart":false});
            fillet(context, id + "F15", {"entities" : qUnion([Q0]), "radius" : 2 * mm, "tangentPropagation" : true, "allowEdgeOverflow" : false});
        }
        {
            var Q0;
            {var subQ0=sQuery(id+"F0.wireOp",EDGE,"E22.filletArc");var subQ1=sQuery(id+"F0.wireOp",EDGE,"E7");var subQ2=sQuery(id+"F0.wireOp",EDGE,"E6");var subQ3=sQuery(id+"F0.wireOp",EDGE,"E5");var subQ4=sQuery(id+"F0.wireOp",EDGE,"E4");var subQ5=sQuery(id+"F0.wireOp",EDGE,"E1.bottom");var subQ6=sQuery(id+"F0.wireOp",EDGE,"E21.filletArc");var subQ7=sQuery(id+"F0.wireOp",EDGE,"E1.top");var subQ8=sQuery(id+"F0.wireOp",EDGE,"E1.left");var subQ9=sQuery(id+"F0.wireOp",EDGE,"E1.right");var subQ10=sQuery(id+"F0.wireOp",EDGE,"E23.filletArc");var subQ11=sQuery(id+"F0.wireOp",EDGE,"E24.filletArc");Q0=makeQuery(id+"F2.boolean.opBoolean","SPLIT",FACE,{"disambiguationData":[TD([makeQuery(id+"F1.opExtrude","SWEPT_FACE",FACE,{"disambiguationData":[OSD([subQ5])]})])],"derivedFrom":makeQuery(id+"F1.opExtrude","CAP_FACE",FACE,{"disambiguationData":[OSD([subQ5,subQ7,subQ8,subQ9,subQ4,subQ3,subQ2,subQ1,subQ6,subQ0,subQ10,subQ11])],"isStart":true})});}
            var sketch = newSketch(context, id + "F16", { "sketchPlane" : qUnion([Q0])});
            skLineSegment(sketch, "E79", {"start": v(-45.86, 90) * mm, "end": v(-30, 105.86) * mm});
            skLineSegment(sketch, "E80", {"start": v(-30, 105.86) * mm, "end": v(-30, 135.86) * mm});
            skLineSegment(sketch, "E81", {"start": v(30, 135.86) * mm, "end": v(30, 105.86) * mm});
            skLineSegment(sketch, "E82", {"start": v(30, 105.86) * mm, "end": v(45.86, 90) * mm});
            skLineSegment(sketch, "E83", {"start": v(-80, 0) * mm, "end": v(80, 0) * mm, "construction": true});
            skLineSegment(sketch, "E84", {"start": v(0, 0) * mm, "end": v(0, 135.86) * mm, "construction": true});
            skPoint(sketch, "E84.endSnap0", {"position": v(0, 90) * mm});
            skLineSegment(sketch, "E85", {"start": v(30, 135.86) * mm, "end": v(0, 135.86) * mm});
            skLineSegment(sketch, "E86", {"start": v(0, 135.86) * mm, "end": v(-30, 135.86) * mm});
            skLineSegment(sketch, "E87.MirrorCS", {"start": v(0, -135.86) * mm, "end": v(-30, -135.86) * mm});
            skLineSegment(sketch, "E88.MirrorCS", {"start": v(30, -135.86) * mm, "end": v(0, -135.86) * mm});
            skLineSegment(sketch, "E89.MirrorCS", {"start": v(-30, -105.86) * mm, "end": v(-30, -135.86) * mm});
            skPoint(sketch, "E90.MirrorP", {"position": v(0, -90) * mm});
            skLineSegment(sketch, "E91.MirrorCS", {"start": v(30, -135.86) * mm, "end": v(30, -105.86) * mm});
            skLineSegment(sketch, "E92.MirrorCS", {"start": v(-45.86, -90) * mm, "end": v(-30, -105.86) * mm});
            skLineSegment(sketch, "E93.MirrorCS", {"start": v(30, -105.86) * mm, "end": v(45.86, -90) * mm});
            skLineSegment(sketch, "E94.MirrorCS", {"start": v(0, 0) * mm, "end": v(0, -135.86) * mm, "construction": true});
            skSolve(sketch);
        }
        {
            var Q0;
            Q0=makeQuery(id+"F16.imprint","IMPRINT",FACE,{"disambiguationData":[TD([[makeQuery(id+"F16.imprint","IMPRINT",EDGE,{"derivedFrom":makeQuery(id+"F1.opExtrude","CAP_EDGE",EDGE,{"disambiguationData":[OSD([sQuery(id+"F0.wireOp",EDGE,"E1.left")])],"isStart":true})}),-1.0]])]});
            var Q1;
            Q1=makeQuery(id+"F16.imprint","IMPRINT",FACE,{"disambiguationData":[TD([[makeQuery(id+"F16.imprint","IMPRINT",EDGE,{"derivedFrom":sQuery(id+"F16.wireOp",EDGE,"E91.MirrorCS")}),1.0]])]});
            var Q2;
            {var subQ1=sQuery(id+"F16.wireOp",EDGE,"E79");Q2=makeQuery(id+"F16.imprint","IMPRINT",FACE,{"disambiguationData":[TD([[makeQuery(id+"F16.imprint","IMPRINT",EDGE,{"derivedFrom":subQ1}),-1.0]])]});}
            var Q3;
            Q3=makeQuery(id+"F2.opExtrude","CAP_FACE",FACE,{"disambiguationData":[OSD([sQuery(id+"F0.wireOp",EDGE,"E12"),sQuery(id+"F0.wireOp",EDGE,"E13"),sQuery(id+"F0.wireOp",EDGE,"E14"),sQuery(id+"F0.wireOp",EDGE,"E15"),sQuery(id+"F0.wireOp",EDGE,"E17.filletArc"),sQuery(id+"F0.wireOp",EDGE,"E18.filletArc"),sQuery(id+"F0.wireOp",EDGE,"E19.filletArc"),sQuery(id+"F0.wireOp",EDGE,"E20.filletArc"),sQuery(id+"F0.wireOp",EDGE,"E25.0"),sQuery(id+"F0.wireOp",EDGE,"E25.1"),sQuery(id+"F0.wireOp",EDGE,"E25.2"),sQuery(id+"F0.wireOp",EDGE,"E25.3"),sQuery(id+"F0.wireOp",EDGE,"E25.4"),sQuery(id+"F0.wireOp",EDGE,"E25.5"),sQuery(id+"F0.wireOp",EDGE,"E25.6"),sQuery(id+"F0.wireOp",EDGE,"E25.7")])],"isStart":false});
            extrude(context, id + "F17", {"entities" : qUnion([Q0, Q1, Q2]), "endBound" : BoundingType.UP_TO_SURFACE, "endBoundEntityFace" : qUnion([Q3]), "depth" : 25 * mm});
        }
    });
